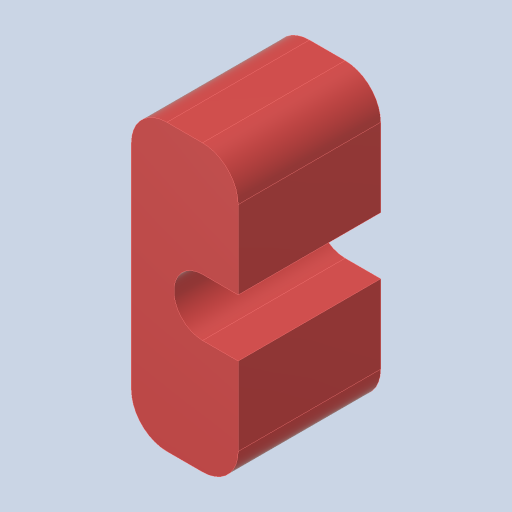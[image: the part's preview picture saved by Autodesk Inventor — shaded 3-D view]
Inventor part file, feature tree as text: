
AUTODESK INVENTOR PART (.ipt)
format: ipt  version: 2023.4 (Build 274418000, 418)  size: 122,368 bytes
history: native  units: in
note: dims shown in document units (in); Inventor stores cm internally (conversion verified against a paired STEP export)
features: extrude x1, fillet x1, sketch x1
ambient origin geometry x8: Origin, YZ Plane, XZ Plane, XY Plane, X Axis, Y Axis, Z Axis, Center Point
bodies: Solid1 (feature_tree)
feature tree (3):
  extrude  "Extrusion1"  Depth=1.0in
  fillet  "Fillet1"  Radius=0.125in
  sketch  "Sketch1"  dims[d0=0.375in d1=1.0in d2=0.125in d3=0.5in d4=0.201in d5=0.5in d6=0.0in d7=0.125in]
